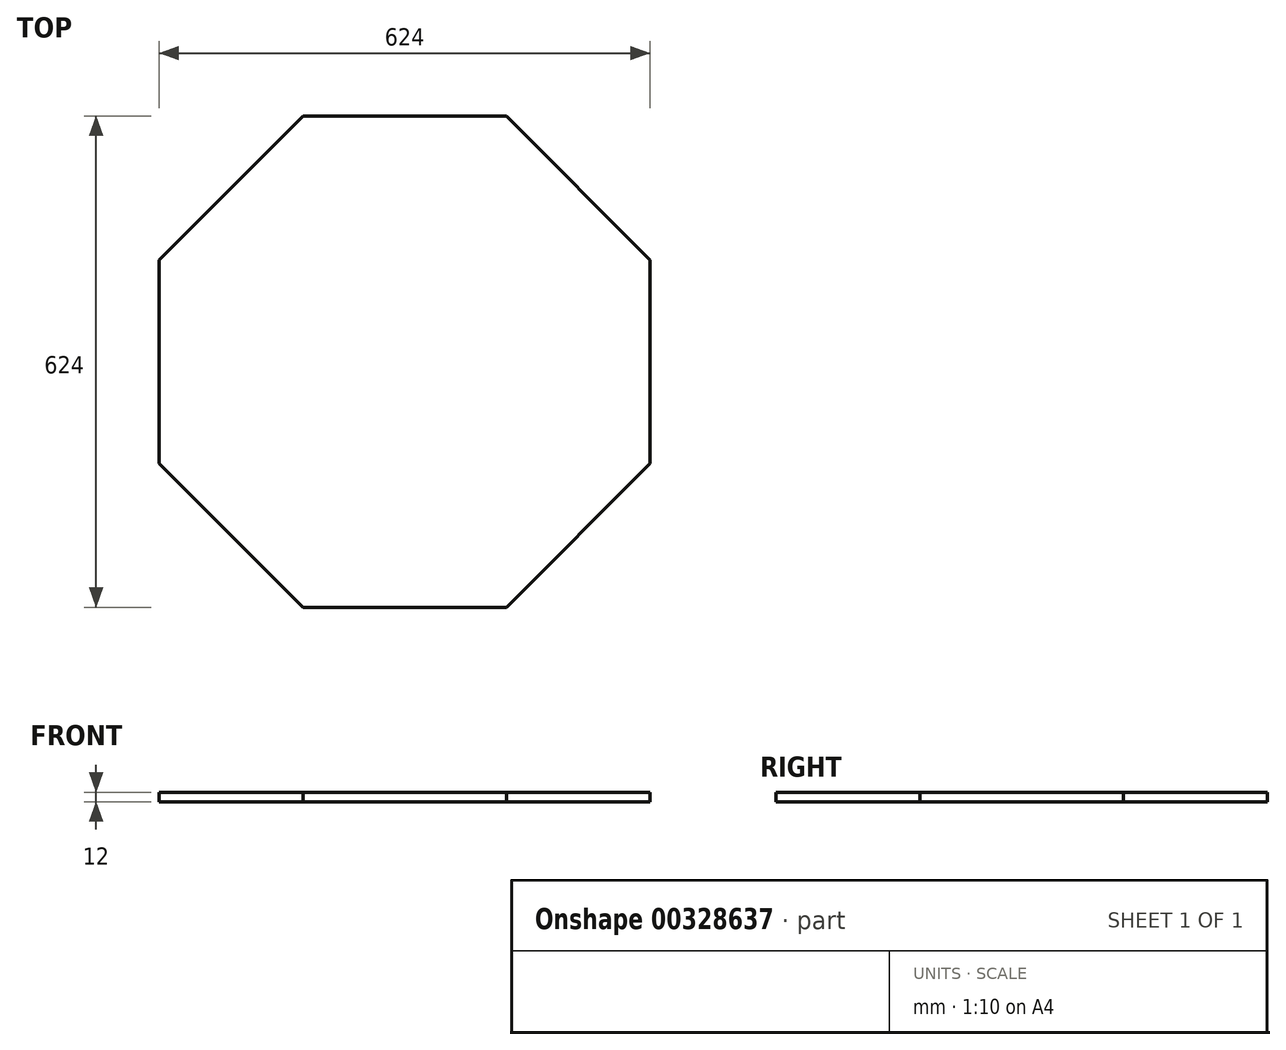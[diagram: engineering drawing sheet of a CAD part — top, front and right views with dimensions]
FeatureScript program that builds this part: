
annotation { "Feature Type Name" : "Feature", "Feature Type Description" : "" }
export const myFeature = defineFeature(function(context is Context, id is Id, definition is map)
    precondition{}
    {
        {
            var Q0;
            Q0=qCreatedBy(makeId("Top.planeOp"),FACE);
            var sketch = newSketch(context, id + "F0", { "sketchPlane" : qUnion([Q0])});
            skCircle(sketch, "E0.cCircle", {"center": v(0, 0) * mm, "radius": 312 * mm, "construction": true});
            skLineSegment(sketch, "E0.0", {"start": v(-129.23, 312) * mm, "end": v(129.23, 312) * mm});
            skLineSegment(sketch, "E0.1", {"start": v(129.23, 312) * mm, "end": v(312, 129.23) * mm});
            skLineSegment(sketch, "E0.2", {"start": v(312, 129.23) * mm, "end": v(312, -129.23) * mm});
            skLineSegment(sketch, "E0.3", {"start": v(312, -129.23) * mm, "end": v(129.23, -312) * mm});
            skLineSegment(sketch, "E0.4", {"start": v(129.23, -312) * mm, "end": v(-129.23, -312) * mm});
            skLineSegment(sketch, "E0.5", {"start": v(-129.23, -312) * mm, "end": v(-312, -129.23) * mm});
            skLineSegment(sketch, "E0.6", {"start": v(-312, -129.23) * mm, "end": v(-312, 129.23) * mm});
            skLineSegment(sketch, "E0.7", {"start": v(-312, 129.23) * mm, "end": v(-129.23, 312) * mm});
            skPoint(sketch, "E0.0.midPoint", {"position": v(0, 312) * mm});
            skSolve(sketch);
        }
        {
            var Q0;
            Q0=qSketchRegion(id+"F0",true);
            extrude(context, id + "F1", {"entities" : qUnion([Q0]), "oppositeDirection" : true, "depth" : 12 * mm});
        }
    });
